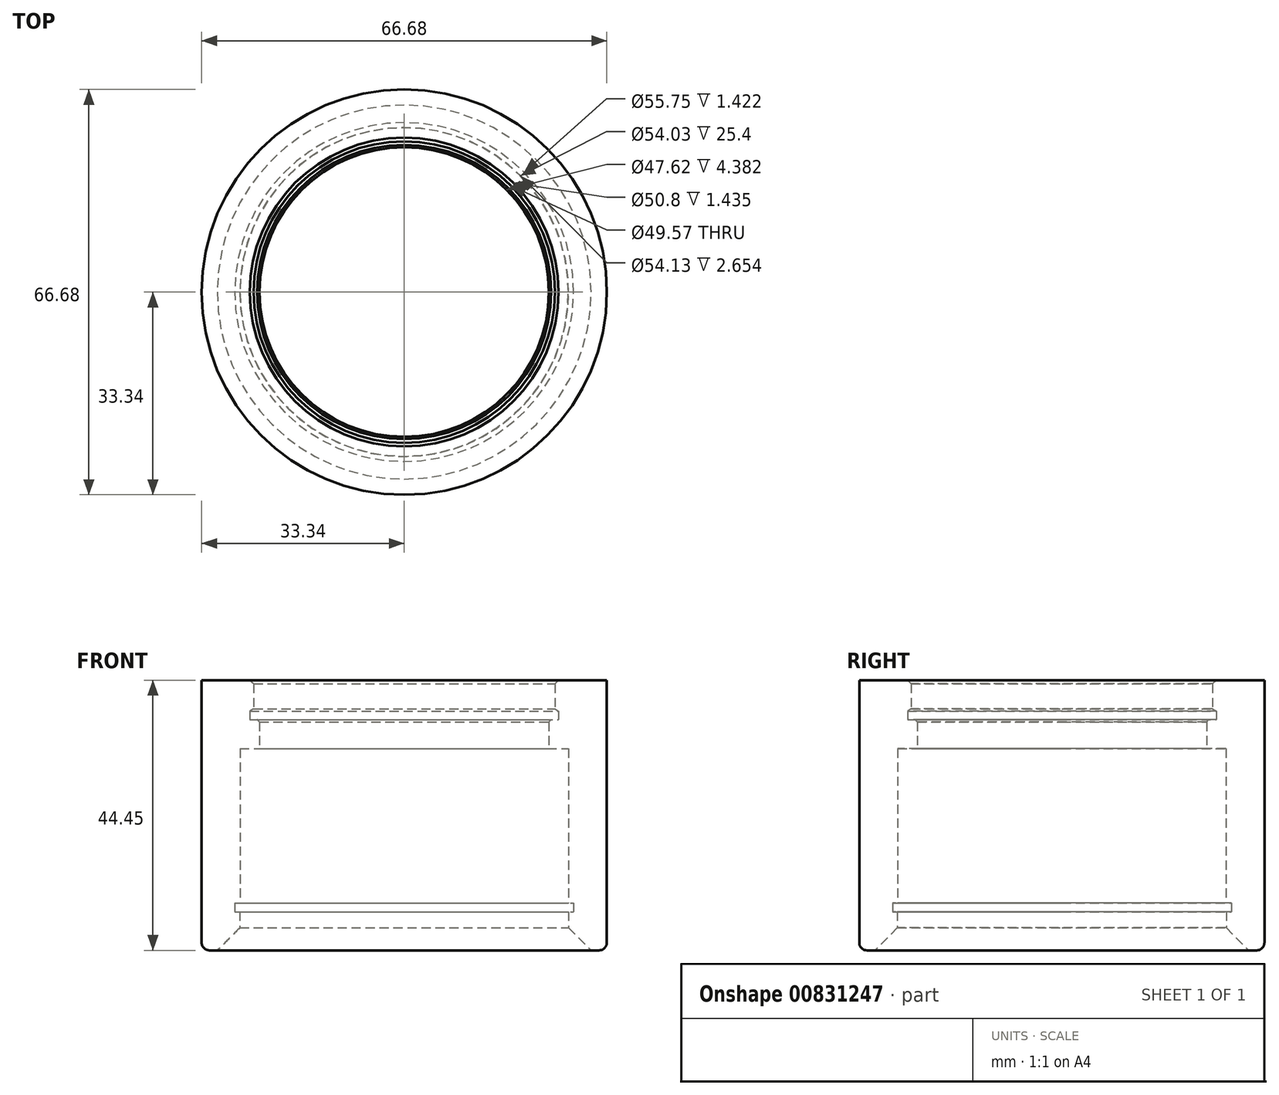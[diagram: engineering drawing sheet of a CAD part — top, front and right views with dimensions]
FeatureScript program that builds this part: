
annotation { "Feature Type Name" : "Feature", "Feature Type Description" : "" }
export const myFeature = defineFeature(function(context is Context, id is Id, definition is map)
    precondition{}
    {
        {
            var Q0;
            Q0=qCreatedBy(makeId("Front.planeOp"),FACE);
            var sketch = newSketch(context, id + "F0", { "sketchPlane" : qUnion([Q0])});
            skLineSegment(sketch, "E0", {"start": v(-33.34, 44.45) * mm, "end": v(-33.34, 0) * mm});
            skLineSegment(sketch, "E1", {"start": v(-33.34, 44.45) * mm, "end": v(-25.4, 44.45) * mm});
            skLineSegment(sketch, "E2", {"start": v(-24.78, 43.83) * mm, "end": v(-24.78, 39.73) * mm});
            skLineSegment(sketch, "E3", {"start": v(-25.4, 37.93) * mm, "end": v(-24.2, 37.93) * mm});
            skLineSegment(sketch, "E4", {"start": v(-23.81, 37.55) * mm, "end": v(-23.81, 33.17) * mm});
            skLineSegment(sketch, "E5", {"start": v(-23.81, 33.17) * mm, "end": v(-27.01, 33.17) * mm});
            skLineSegment(sketch, "E6", {"start": v(-27.01, 33.17) * mm, "end": v(-27.01, 7.77) * mm});
            skLineSegment(sketch, "E7", {"start": v(-27.01, 7.77) * mm, "end": v(-27.88, 7.77) * mm});
            skLineSegment(sketch, "E8", {"start": v(-27.88, 7.77) * mm, "end": v(-27.88, 6.35) * mm});
            skLineSegment(sketch, "E9", {"start": v(-27.88, 6.35) * mm, "end": v(-27.06, 6.35) * mm});
            skLineSegment(sketch, "E10", {"start": v(-27.06, 6.35) * mm, "end": v(-27.06, 3.7) * mm});
            skLineSegment(sketch, "E11", {"start": v(-27.06, 3.7) * mm, "end": v(-30.76, 0) * mm});
            skLineSegment(sketch, "E12", {"start": v(-30.76, 0) * mm, "end": v(-33.34, 0) * mm});
            skLineSegment(sketch, "E13", {"start": v(0, 0) * mm, "end": v(0, 24.7) * mm, "construction": true});
            skLineSegment(sketch, "E14", {"start": v(-25.4, 39.37) * mm, "end": v(-25.4, 37.93) * mm});
            skLineSegment(sketch, "E15", {"start": v(-25.4, 44.45) * mm, "end": v(-24.78, 43.83) * mm});
            skLineSegment(sketch, "E16", {"start": v(-25.4, 39.37) * mm, "end": v(-24.78, 39.73) * mm});
            skLineSegment(sketch, "E17", {"start": v(-24.2, 37.93) * mm, "end": v(-23.81, 37.55) * mm});
            skSolve(sketch);
        }
        {
            var Q0;
            Q0 = qSketchRegion(id + "F0", true);
            var Q1;
            Q1=sQuery(id+"F0.wireOp",EDGE,"E13");
            revolve(context, id + "F1", {"surfaceOperationType" : NewSurfaceOperationType.NEW, "entities" : qUnion([Q0]), "axis" : qUnion([Q1]), "revolveType" : RevolveType.FULL});
        }
        {
            var Q0;
            Q0=makeQuery(id+"F1.opRevolve","SWEPT_FACE",FACE,{"disambiguationData":[OSD([sQuery(id+"F0.wireOp",EDGE,"E1")])]});
            var sketch = newSketch(context, id + "F2", { "sketchPlane" : qUnion([Q0])});
            skCircle(sketch, "E18.0", {"center": v(0, 0) * mm, "radius": 24.78 * mm});
            skSolve(sketch);
        }
        {
            var Q0;
            Q0=qCreatedBy(makeId("Front.planeOp"),FACE);
            var sketch = newSketch(context, id + "F3", { "sketchPlane" : qUnion([Q0])});
            skLineSegment(sketch, "E19", {"start": v(24.8, 45.31) * mm, "end": v(25.4, 44.96) * mm});
            skLineSegment(sketch, "E20", {"start": v(24.8, 45.31) * mm, "end": v(24.8, 44.45) * mm});
            skLineSegment(sketch, "E21", {"start": v(25.4, 44.8) * mm, "end": v(24.8, 44.45) * mm});
            skLineSegment(sketch, "E22", {"start": v(25.4, 44.8) * mm, "end": v(25.4, 44.96) * mm});
            skLineSegment(sketch, "E23", {"start": v(0, 0) * mm, "end": v(0, 175.94) * mm, "construction": true});
            skLineSegment(sketch, "E24", {"start": v(25.4, 44.88) * mm, "end": v(24.8, 44.88) * mm, "construction": true});
            skSolve(sketch);
        }
        {
            var Q0;
            Q0=makeQuery(id+"F1.opRevolve","SWEPT_EDGE",EDGE,{"disambiguationData":[OSD([sQuery(id+"F0.wireOp",EDGE,"E0"),sQuery(id+"F0.wireOp",EDGE,"E12")])]});
            fillet(context, id + "F4", {"entities" : qUnion([Q0]), "radius" : 1.27 * mm, "tangentPropagation" : true, "allowEdgeOverflow" : false});
        }
    });
